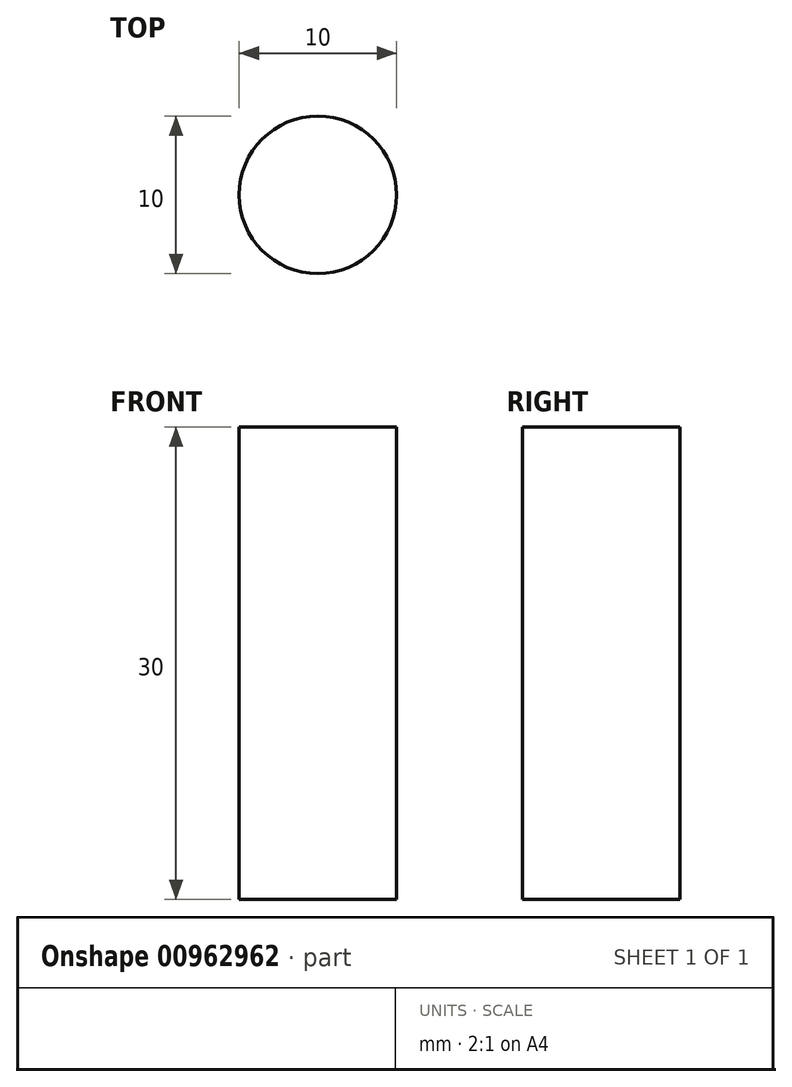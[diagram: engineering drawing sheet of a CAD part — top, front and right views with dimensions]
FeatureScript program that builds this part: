
annotation { "Feature Type Name" : "Feature", "Feature Type Description" : "" }
export const myFeature = defineFeature(function(context is Context, id is Id, definition is map)
    precondition{}
    {
        {
            var Q0;
            Q0=qCreatedBy(makeId("Top.planeOp"),FACE);
            var sketch = newSketch(context, id + "F0", { "sketchPlane" : qUnion([Q0])});
            skCircle(sketch, "E0", {"center": v(0, 0) * mm, "radius": 5 * mm});
            skSolve(sketch);
        }
        {
            var Q0;
            Q0 = qSketchRegion(id + "F0", true);
            extrude(context, id + "F1", {"entities" : qUnion([Q0]), "depth" : 30 * mm, "offsetDistance" : 25 * mm, "symmetric" : true});
        }
    });
